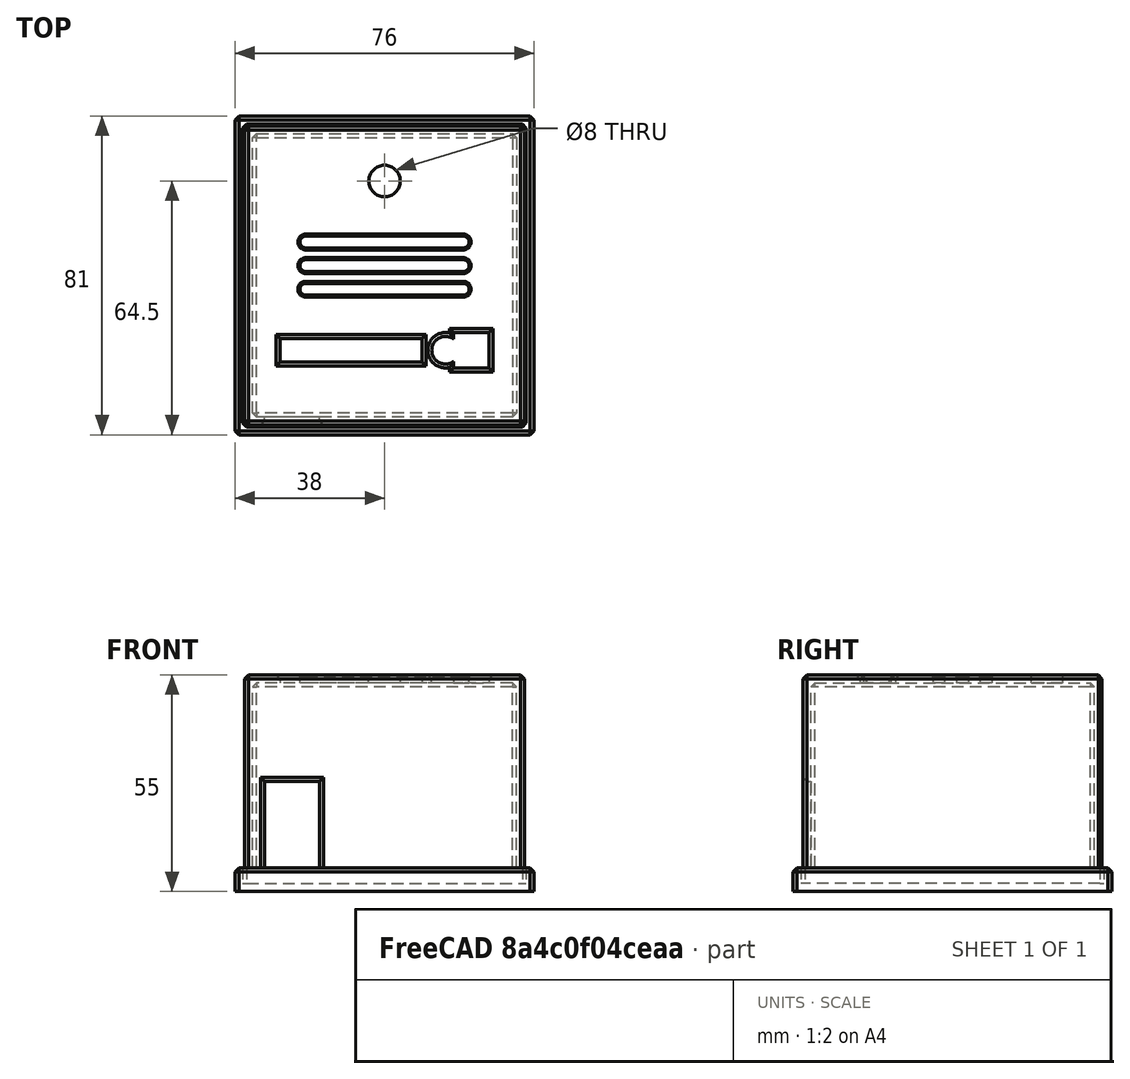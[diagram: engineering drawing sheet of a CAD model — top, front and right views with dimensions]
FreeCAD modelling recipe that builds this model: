
FCSTD DOCUMENT  (FreeCAD 0.17R13541 (Git))
Label: TrashParrotRecorderBox
License: All rights reserved
LicenseURL: http://en.wikipedia.org/wiki/All_rights_reserved
objects: Sketcher::SketchObject×7, TechDraw::DrawViewDimension×6, PartDesign::Pocket×5, PartDesign::Chamfer×3, PartDesign::Pad×2, PartDesign::Body×2, TechDraw::DrawViewPart×2, Mesh::Feature×2, PartDesign::ShapeBinder×1, TechDraw::DrawSVGTemplate×1, TechDraw::DrawPage×1
note: 27 computed .brp shape members not serialized (recipe doc carries the construction recipe); baked Part::Feature solids carry a one-line shape summary decoded from their .brp

FEATURE [Sketcher::SketchObject] Sketch
  MapMode = 5
  Support = -> [XY_Plane]
  sketch-geometry (4):
    g0: LineSegment StartX=-35.5 StartY=38 StartZ=0 EndX=35.5 EndY=38 EndZ=0
    g1: LineSegment StartX=35.5 StartY=38 StartZ=0 EndX=35.5 EndY=-38 EndZ=0
    g2: LineSegment StartX=35.5 StartY=-38 StartZ=0 EndX=-35.5 EndY=-38 EndZ=0
    g3: LineSegment StartX=-35.5 StartY=-38 StartZ=0 EndX=-35.5 EndY=38 EndZ=0
  constraints (12):
    c: Coincident(g0,g1)
    c: Coincident(g1,g2)
    c: Coincident(g2,g3)
    c: Coincident(g3,g0)
    c: Horizontal(g0)
    c: Horizontal(g2)
    c: Vertical(g1)
    c: Vertical(g3)
    c: Distance(g0) = 71
    c: Distance(g3) = 76
    c: Symmetric(g0,g0,g-2)
    c: Symmetric(g1,g0,g-1)
FEATURE [PartDesign::Pad] Pad
  Length = 49
  Length2 = 100
  Profile = -> Sketch
  Type = 0
FEATURE [Sketcher::SketchObject] Sketch001
  ExternalGeometry = -> [Pad]
  MapMode = 5
  Placement = pos=(0,0,0) rot=(1,0,0;3.14159rad)
  Support = -> [Pad]
  sketch-geometry (4):
    g0: LineSegment StartX=33.5 StartY=36 StartZ=0 EndX=-33.5 EndY=36 EndZ=0
    g1: LineSegment StartX=-33.5 StartY=36 StartZ=0 EndX=-33.5 EndY=-36 EndZ=0
    g2: LineSegment StartX=-33.5 StartY=-36 StartZ=0 EndX=33.5 EndY=-36 EndZ=0
    g3: LineSegment StartX=33.5 StartY=-36 StartZ=0 EndX=33.5 EndY=36 EndZ=0
  constraints (12):
    c: Coincident(g0,g1)
    c: Coincident(g1,g2)
    c: Coincident(g2,g3)
    c: Coincident(g3,g0)
    c: Horizontal(g0)
    c: Horizontal(g2)
    c: Vertical(g1)
    c: Vertical(g3)
    c: DistanceY(g-6,g1) = 2
    c: DistanceX(g-6,g1) = 2
    c: DistanceY(g0,g-4) = 2
    c: DistanceX(g0,g-4) = 2
FEATURE [PartDesign::Pocket] Pocket
  BaseFeature = -> Pad
  Length = 47
  Length2 = 100
  Profile = -> Sketch001
  Type = 0
FEATURE [Sketcher::SketchObject] Sketch002
  ExternalGeometry = -> [Pocket]
  MapMode = 5
  Placement = pos=(0,-38,0) rot=(1,0,0;1.5708rad)
  Support = -> [Pocket]
  sketch-geometry (5):
    g0: LineSegment StartX=-30.5 StartY=0 StartZ=0 EndX=-16.5 EndY=0 EndZ=0
    g1: LineSegment StartX=-16.5 StartY=0 StartZ=0 EndX=-16.5 EndY=22 EndZ=0
    g2: LineSegment StartX=-16.5 StartY=22 StartZ=0 EndX=-30.5 EndY=22 EndZ=0
    g3: LineSegment StartX=-30.5 StartY=22 StartZ=0 EndX=-30.5 EndY=0 EndZ=0
    g4: GeomPoint X=-23.5 Y=22 Z=0
  constraints (14):
    c: Coincident(g0,g1)
    c: Coincident(g1,g2)
    c: Coincident(g2,g3)
    c: Coincident(g3,g0)
    c: Horizontal(g0)
    c: Horizontal(g2)
    c: Vertical(g1)
    c: Vertical(g3)
    c: PointOnObject(g0,g-1)
    c: Distance(g1) = 22
    c: Distance(g2) = 14
    c: PointOnObject(g4,g2)
    c: Distance(g4,g-3) = 12
    c: Distance(g4,g2) = 7
FEATURE [PartDesign::Pocket] Pocket001
  BaseFeature = -> Pocket
  Length = 5
  Length2 = 100
  Profile = -> Sketch002
  Type = 2
FEATURE [Sketcher::SketchObject] Sketch003
  ExternalGeometry = -> [Pocket001]
  MapMode = 5
  Placement = pos=(0,0,49) rot=(0,0,1;0rad)
  Support = -> [Pocket001]
  sketch-geometry (16):
    g0: Circle CenterX=0 CenterY=24 CenterZ=0 NormalX=0 NormalY=0 NormalZ=1 AngleXU=0 Radius=4
    g1: LineSegment StartX=9.5 StartY=-22 StartZ=0 EndX=-26.5 EndY=-22 EndZ=0
    g2: LineSegment StartX=-26.5 StartY=-22 StartZ=0 EndX=-26.5 EndY=-16 EndZ=0
    g3: LineSegment StartX=-26.5 StartY=-16 StartZ=0 EndX=9.5 EndY=-16 EndZ=0
    g4: LineSegment StartX=9.5 StartY=-16 StartZ=0 EndX=9.5 EndY=-22 EndZ=0
    g5: LineSegment [constr] StartX=12 StartY=-19 StartZ=0 EndX=9.5 EndY=-19 EndZ=0
    g6: LineSegment StartX=26.5 StartY=-23.5 StartZ=0 EndX=17.5 EndY=-23.5 EndZ=0
    g7: LineSegment StartX=17.5 StartY=-14.5 StartZ=0 EndX=26.5 EndY=-14.5 EndZ=0
    g8: LineSegment StartX=26.5 StartY=-14.5 StartZ=0 EndX=26.5 EndY=-23.5 EndZ=0
    g9: LineSegment [constr] StartX=22 StartY=-23.5 StartZ=0 EndX=22 EndY=-14.5 EndZ=0
    g10: LineSegment [constr] StartX=26.5 StartY=-19 StartZ=0 EndX=17.5 EndY=-19 EndZ=0
    g11: GeomPoint X=26.5 Y=-16 Z=0
    g12: GeomPoint X=15.5 Y=-19 Z=0
    g13: ArcOfCircle CenterX=15.5 CenterY=-19 CenterZ=0 NormalX=0 NormalY=0 NormalZ=1 AngleXU=0 Radius=3.5 StartAngle=0.962551 EndAngle=5.32063
    g14: LineSegment StartX=17.5 StartY=-14.5 StartZ=0 EndX=17.5 EndY=-16.1277 EndZ=0
    g15: LineSegment StartX=17.5 StartY=-23.5 StartZ=0 EndX=17.5 EndY=-21.8723 EndZ=0
  constraints (48):
    c: Coincident(g1,g2)
    c: Coincident(g2,g3)
    c: Coincident(g3,g4)
    c: Coincident(g4,g1)
    c: Horizontal(g1)
    c: Horizontal(g3)
    c: Vertical(g2)
    c: Vertical(g4)
    c: Distance(g4) = 6
    c: Distance(g1) = 36
    c: PointOnObject(g0,g-2)
    c: Radius(g0) = 4
    c: Distance(g0,g-3) = 14
    c: PointOnObject(g5,g4)
    c: Horizontal(g5)
    c: Distance(g5) = 2.5
    c: Symmetric(g3,g1,g5)
    c: Coincident(g7,g8)
    c: Coincident(g8,g6)
    c: Horizontal(g6)
    c: Horizontal(g7)
    c: Vertical(g8)
    c: PointOnObject(g9,g6)
    c: PointOnObject(g9,g7)
    c: Vertical(g9)
    c: PointOnObject(g10,g8)
    c: Horizontal(g10)
    c: Symmetric(g6,g6,g9)
    c: Symmetric(g7,g6,g10)
    c: Horizontal(g5,g10)
    c: Distance(g6) = 9
    c: Distance(g8) = 9
    c: PointOnObject(g11,g8)
    c: Symmetric(g11,g2,g-2)
    c: Distance(g1,g-4) = 16
    c: Distance(g12,g9) = 6.5
    c: Horizontal(g10,g12)
    c: Coincident(g13,g12)
    c: Radius(g13) = 3.5
    c: Vertical(g7,g13)
    c: Vertical(g6,g13)
    c: Vertical(g13,g10)
    c: PointOnObject(g5,g13)
    c: Coincident(g14,g7)
    c: Coincident(g14,g13)
    c: Coincident(g15,g6)
    c: Coincident(g15,g13)
    c: Vertical(g13,g10)
FEATURE [PartDesign::Pocket] Pocket002
  BaseFeature = -> Pocket001
  Length = 5
  Length2 = 100
  Profile = -> Sketch003
  Type = 1
FEATURE [PartDesign::Chamfer] Chamfer
  Base = -> Pocket002 [Edge27,Edge29,Edge28,Edge30,Edge25,Edge26,Edge24,Edge21,Edge23,Edge22,Edge3,Edge18,Edge19,Edge7,Edge40,Edge46,Edge43,Edge44,Edge5,Edge1,Edge31,Edge4,Edge41,Edge45,Edge42,Edge39,Edge33,Edge34,Edge32]
  BaseFeature = -> Pocket002
  Size = 1
FEATURE [Sketcher::SketchObject] Sketch004
  ExternalGeometry = -> [Chamfer]
  MapMode = 5
  Placement = pos=(0,0,49) rot=(0,0,1;0rad)
  Support = -> [Chamfer]
  sketch-geometry (14):
    g0: ArcOfCircle CenterX=-20 CenterY=8.5 CenterZ=0 NormalX=0 NormalY=0 NormalZ=1 AngleXU=0 Radius=1.5 StartAngle=1.5708 EndAngle=4.71239
    g1: ArcOfCircle CenterX=20 CenterY=8.5 CenterZ=0 NormalX=0 NormalY=0 NormalZ=1 AngleXU=0 Radius=1.5 StartAngle=4.71239 EndAngle=7.85398
    g2: LineSegment StartX=-20 StartY=7 StartZ=0 EndX=20 EndY=7 EndZ=0
    g3: LineSegment StartX=-20 StartY=10 StartZ=0 EndX=20 EndY=10 EndZ=0
    g4: ArcOfCircle CenterX=-20 CenterY=2.5 CenterZ=0 NormalX=0 NormalY=0 NormalZ=1 AngleXU=0 Radius=1.5 StartAngle=1.5708 EndAngle=4.71239
    g5: ArcOfCircle CenterX=20 CenterY=2.5 CenterZ=0 NormalX=0 NormalY=0 NormalZ=1 AngleXU=0 Radius=1.5 StartAngle=4.71239 EndAngle=7.85398
    g6: LineSegment StartX=-20 StartY=1 StartZ=0 EndX=20 EndY=1 EndZ=0
    g7: LineSegment StartX=-20 StartY=4 StartZ=0 EndX=20 EndY=4 EndZ=0
    g8: ArcOfCircle CenterX=-20 CenterY=-3.5 CenterZ=0 NormalX=0 NormalY=0 NormalZ=1 AngleXU=0 Radius=1.5 StartAngle=1.5708 EndAngle=4.71239
    g9: ArcOfCircle CenterX=20 CenterY=-3.5 CenterZ=0 NormalX=0 NormalY=0 NormalZ=1 AngleXU=0 Radius=1.5 StartAngle=4.71239 EndAngle=7.85398
    g10: LineSegment StartX=-20 StartY=-5 StartZ=0 EndX=20 EndY=-5 EndZ=0
    g11: LineSegment StartX=-20 StartY=-2 StartZ=0 EndX=20 EndY=-2 EndZ=0
    g12: LineSegment [constr] StartX=20 StartY=20 StartZ=0 EndX=-27.5 EndY=20 EndZ=0
    g13: LineSegment [constr] StartX=20 StartY=2.5 StartZ=0 EndX=-20 EndY=2.5 EndZ=0
  constraints (35):
    c: Tangent(g0,g3) = 1.5708
    c: Tangent(g0,g2) = -1.5708
    c: Tangent(g2,g1) = -1.5708
    c: Tangent(g3,g1) = 1.5708
    c: Horizontal(g2)
    c: Equal(g0,g1)
    c: Symmetric(g1,g0,g-2)
    c: Distance(g3) = 40
    c: Tangent(g4,g7) = 1.5708
    c: Tangent(g4,g6) = -1.5708
    c: Tangent(g6,g5) = -1.5708
    c: Tangent(g7,g5) = 1.5708
    c: Horizontal(g6)
    c: Equal(g4,g5)
    c: Equal(g3,g7) = 40
    c: Equal(g0,g4) = 1.5
    c: Tangent(g8,g11) = 1.5708
    c: Tangent(g8,g10) = -1.5708
    c: Tangent(g10,g9) = -1.5708
    c: Tangent(g11,g9) = 1.5708
    c: Horizontal(g10)
    c: Equal(g8,g9)
    c: Distance(g1,g1) = 3
    c: Distance(g1,g5) = 3
    c: Distance(g9,g9) = 3
    c: Vertical(g1,g5)
    c: Vertical(g9,g5)
    c: Vertical(g4,g8)
    c: Distance(g5,g9) = 3
    c: Horizontal(g12)
    c: Tangent(g12,g-4)
    c: Coincident(g13,g5)
    c: Coincident(g13,g4)
    c: Symmetric(g12,g-3,g13)
    c: Vertical(g12,g5)
FEATURE [PartDesign::Pocket] Pocket003
  BaseFeature = -> Chamfer
  Length = 5
  Length2 = 100
  Profile = -> Sketch004
  Type = 1
FEATURE [PartDesign::Chamfer] Chamfer001
  Base = -> Pocket003 [Edge91,Edge87,Edge95]
  BaseFeature = -> Pocket003
  Size = 0.5
FEATURE [PartDesign::Body] Body
  Group = -> [Sketch,Pad,Sketch001,Pocket,Sketch002,Pocket001,Sketch003,Pocket002,Chamfer,Sketch004,Pocket003,Chamfer001]
  Origin = -> Origin
  Tip = -> Chamfer001
FEATURE [PartDesign::ShapeBinder] CopyChamfer001
FEATURE [Sketcher::SketchObject] Sketch005
  MapMode = 5
  Placement = pos=(0,0,0) rot=(1,0,0;3.14159rad)
  Support = -> [CopyChamfer001]
  expr: Constraints[9] = 80 + 1
  expr: Constraints[8] = 75 + 1
  sketch-geometry (4):
    g0: LineSegment StartX=-38 StartY=40.5 StartZ=0 EndX=38 EndY=40.5 EndZ=0
    g1: LineSegment StartX=38 StartY=40.5 StartZ=0 EndX=38 EndY=-40.5 EndZ=0
    g2: LineSegment StartX=38 StartY=-40.5 StartZ=0 EndX=-38 EndY=-40.5 EndZ=0
    g3: LineSegment StartX=-38 StartY=-40.5 StartZ=0 EndX=-38 EndY=40.5 EndZ=0
  constraints (12):
    c: Coincident(g0,g1)
    c: Coincident(g1,g2)
    c: Coincident(g2,g3)
    c: Coincident(g3,g0)
    c: Horizontal(g0)
    c: Horizontal(g2)
    c: Vertical(g1)
    c: Vertical(g3)
    c: Distance(g0) = 76
    c: Distance(g3) = 81
    c: Symmetric(g0,g0,g-2)
    c: Symmetric(g0,g1,g-1)
FEATURE [PartDesign::Pad] Pad001
  Length = 6
  Length2 = 100
  Profile = -> Sketch005
  Type = 0
FEATURE [Sketcher::SketchObject] Sketch006
  ExternalGeometry = -> [Pad001]
  MapMode = 5
  Support = -> [Pad001]
  sketch-geometry (4):
    g0: LineSegment StartX=-36 StartY=38.5 StartZ=0 EndX=36 EndY=38.5 EndZ=0
    g1: LineSegment StartX=36 StartY=38.5 StartZ=0 EndX=36 EndY=-38.5 EndZ=0
    g2: LineSegment StartX=36 StartY=-38.5 StartZ=0 EndX=-36 EndY=-38.5 EndZ=0
    g3: LineSegment StartX=-36 StartY=-38.5 StartZ=0 EndX=-36 EndY=38.5 EndZ=0
  constraints (12):
    c: Coincident(g0,g1)
    c: Coincident(g1,g2)
    c: Coincident(g2,g3)
    c: Coincident(g3,g0)
    c: Horizontal(g0)
    c: Horizontal(g2)
    c: Vertical(g1)
    c: Vertical(g3)
    c: DistanceY(g-6,g1) = 2
    c: DistanceX(g1,g-6) = 2
    c: DistanceX(g-4,g0) = 2
    c: DistanceY(g0,g-4) = 2
FEATURE [PartDesign::Pocket] Pocket004
  BaseFeature = -> Pad001
  Length = 0
  Length2 = 100
  Offset = -2
  Profile = -> Sketch006
  Type = 3
  UpToFace = -> Pad001 [Face6]
FEATURE [PartDesign::Chamfer] Chamfer002
  Base = -> Pocket004 [Edge21,Edge19,Edge17,Edge23,Edge2,Edge1,Edge8,Edge5,Edge11,Edge6,Edge3,Edge9]
  BaseFeature = -> Pocket004
  Size = 1
FEATURE [PartDesign::Body] Body001
  Group = -> [CopyChamfer001,Sketch005,Pad001,Sketch006,Pocket004,Chamfer002]
  Origin = -> Origin001
  Tip = -> Chamfer002
FEATURE [TechDraw::DrawSVGTemplate] Template
  EditableTexts = Designed_by_Name=AAAAAAAAAAAAAAAAAAAAAAAAAAAAAAAAAAAAAAAAAa; Drawing_number=111111111111111111111111111111111111111111; FC-Date=TODAY; FC-SC=1:!; FC-SH=Sheet; FC-Title=RIP; Subtitle=Subtitle; Weight=None
  Height = 210
  Orientation = 1
  Width = 297
FEATURE [TechDraw::DrawViewPart] View
  CoarseView = false
  Direction = (0,0,1)
  Focus = 100
  HardHidden = false
  IsoCount = 0
  IsoHidden = false
  IsoVisible = false
  LockPosition = false
  Perspective = false
  Rotation = 0
  ScaleType = 0
  SeamHidden = false
  SeamVisible = false
  SmoothHidden = false
  SmoothVisible = false
  Source = -> [Body]
  X = 67.9967
  Y = 143.938
FEATURE [TechDraw::DrawViewPart] View001
  CoarseView = false
  Direction = (0,0,1)
  Focus = 100
  HardHidden = false
  IsoCount = 0
  IsoHidden = false
  IsoVisible = false
  LockPosition = false
  Perspective = false
  Rotation = 0
  ScaleType = 0
  SeamHidden = false
  SeamVisible = false
  SmoothHidden = false
  SmoothVisible = false
  Source = -> [Body001]
  X = 216.176
  Y = 143.243
FEATURE [TechDraw::DrawViewDimension] Dimension
  FormatSpec = %.2f
  LockPosition = false
  MeasureType = 1
  References2D = -> [View001]
  Rotation = 0
  ScaleType = 0
  Type = 2
  X = -50.6646
  Y = 15.6646
FEATURE [TechDraw::DrawViewDimension] Dimension001
  FormatSpec = %.2f
  LockPosition = false
  MeasureType = 1
  References2D = -> [View001]
  Rotation = 0
  ScaleType = 0
  Type = 1
  X = -14.8287
  Y = 49.8287
FEATURE [TechDraw::DrawViewDimension] Dimension002
  FormatSpec = %.2f
  LockPosition = false
  MeasureType = 1
  References2D = -> [View001]
  Rotation = 0
  ScaleType = 0
  Type = 1
  X = -7.26895
  Y = 24.351
FEATURE [TechDraw::DrawViewDimension] Dimension003
  FormatSpec = %.2f
  LockPosition = false
  MeasureType = 1
  References2D = -> [View001]
  Rotation = 0
  ScaleType = 0
  Type = 2
  X = -26.7134
  Y = 7.45068
FEATURE [TechDraw::DrawViewDimension] Dimension004
  FormatSpec = %.2f
  LockPosition = false
  MeasureType = 1
  References2D = -> [View]
  Rotation = 0
  ScaleType = 0
  Type = 1
  X = -15.0259
  Y = 44.2886
FEATURE [TechDraw::DrawViewDimension] Dimension005
  FormatSpec = %.2f
  LockPosition = false
  MeasureType = 1
  References2D = -> [View]
  Rotation = 0
  ScaleType = 0
  Type = 2
  X = -43.1978
  Y = 16.3236
FEATURE [TechDraw::DrawPage] Page
  KeepUpdated = true
  ProjectionType = 0
  Template = -> Template
  Views = -> [View,View001,Dimension,Dimension001,Dimension002,Dimension003,Dimension004,Dimension005]
FEATURE [Mesh::Feature] Mesh  label="Body (Meshed)"
FEATURE [Mesh::Feature] Mesh001  label="Body001 (Meshed)"
